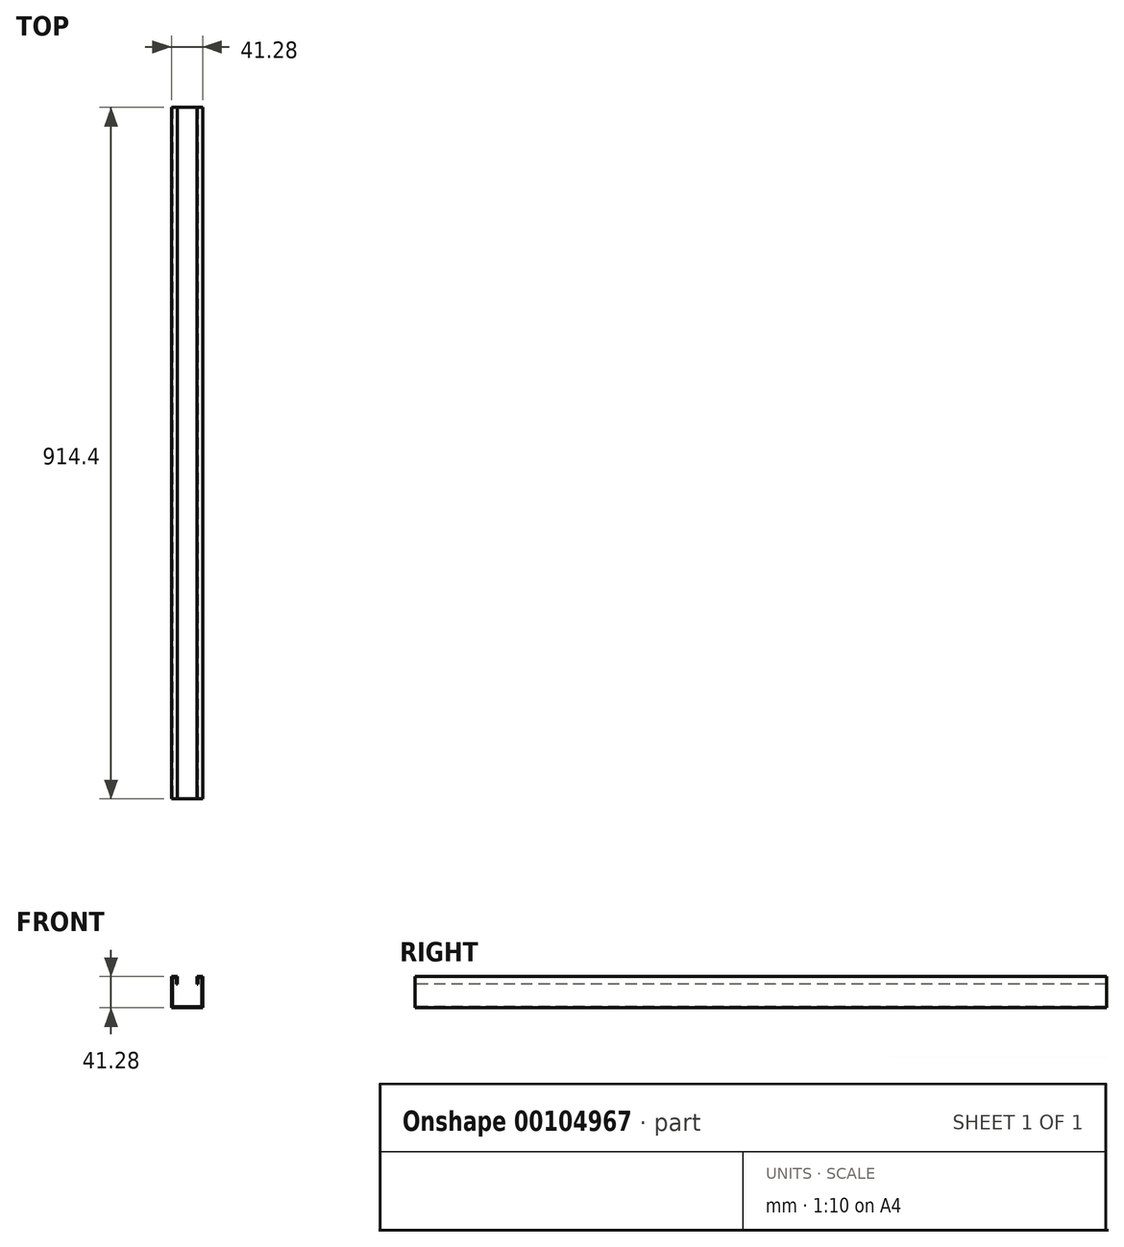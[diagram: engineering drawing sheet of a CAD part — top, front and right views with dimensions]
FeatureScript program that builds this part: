
annotation { "Feature Type Name" : "Feature", "Feature Type Description" : "" }
export const myFeature = defineFeature(function(context is Context, id is Id, definition is map)
    precondition{}
    {
        {
            var Q0;
            Q0=qCreatedBy(makeId("Front.planeOp"),FACE);
            var sketch = newSketch(context, id + "F0", { "sketchPlane" : qUnion([Q0])});
            skLineSegment(sketch, "E0.bottom", {"start": v(-20.64, 20.64) * mm, "end": v(-13.02, 20.64) * mm});
            skLineSegment(sketch, "E0.top", {"start": v(-20.64, -20.64) * mm, "end": v(20.64, -20.64) * mm});
            skLineSegment(sketch, "E0.left", {"start": v(-20.64, 20.64) * mm, "end": v(-20.64, -20.64) * mm});
            skLineSegment(sketch, "E0.right", {"start": v(20.64, 20.64) * mm, "end": v(20.64, -20.64) * mm});
            skLineSegment(sketch, "E1.bottom", {"start": v(-19.37, 19.37) * mm, "end": v(-14.29, 19.37) * mm});
            skLineSegment(sketch, "E1.top", {"start": v(-19.37, -19.37) * mm, "end": v(19.37, -19.37) * mm});
            skLineSegment(sketch, "E1.left", {"start": v(-19.37, 19.37) * mm, "end": v(-19.37, -19.37) * mm});
            skLineSegment(sketch, "E1.right", {"start": v(19.37, 19.37) * mm, "end": v(19.37, -19.37) * mm});
            skLineSegment(sketch, "E2.top", {"start": v(-14.29, 10.48) * mm, "end": v(-13.02, 10.48) * mm});
            skLineSegment(sketch, "E2.left", {"start": v(-14.29, 19.37) * mm, "end": v(-14.29, 10.48) * mm});
            skLineSegment(sketch, "E2.right", {"start": v(-13.02, 20.64) * mm, "end": v(-13.02, 10.48) * mm});
            skLineSegment(sketch, "E3.top", {"start": v(13.02, 10.48) * mm, "end": v(14.29, 10.48) * mm});
            skLineSegment(sketch, "E3.left", {"start": v(13.02, 20.64) * mm, "end": v(13.02, 10.48) * mm});
            skLineSegment(sketch, "E3.right", {"start": v(14.29, 19.37) * mm, "end": v(14.29, 10.48) * mm});
            skLineSegment(sketch, "E4.trimOffspring", {"start": v(14.29, 19.37) * mm, "end": v(19.37, 19.37) * mm});
            skLineSegment(sketch, "E5", {"start": v(13.02, 20.64) * mm, "end": v(20.64, 20.64) * mm});
            skSolve(sketch);
        }
        {
            var Q0;
            Q0 = qSketchRegion(id + "F0", true);
            extrude(context, id + "F1", {"entities" : qUnion([Q0]), "oppositeDirection" : true, "depth" : 914.4 * mm});
        }
    });
